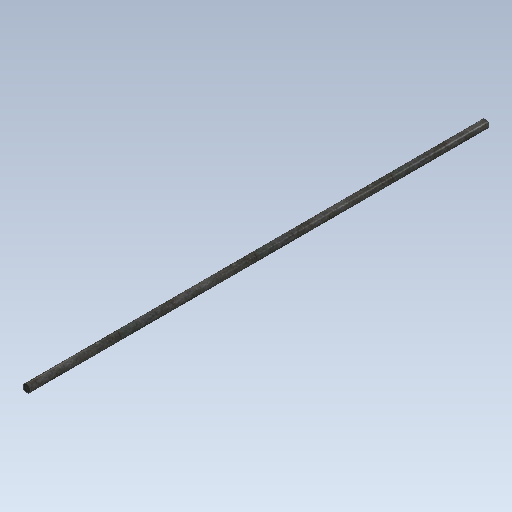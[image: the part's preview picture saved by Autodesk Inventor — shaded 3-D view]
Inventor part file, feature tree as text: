
AUTODESK INVENTOR PART (.ipt)
format: ipt  version: 2020 (Build 240168000, 168)  size: 121,856 bytes
history: native  units: mm
features: extrude x1, sketch x1
ambient origin geometry x8: Origin, YZ Plane, XZ Plane, XY Plane, X Axis, Y Axis, Z Axis, Center Point
bodies: Solid1 (feature_tree)
feature tree (2):
  extrude  "Extrusion1"  Depth=590.0mm TaperAngle=0.0deg
  sketch  "Sketch1"  dims[d0=10.0mm d1=590.0mm d2=0.0mm]
